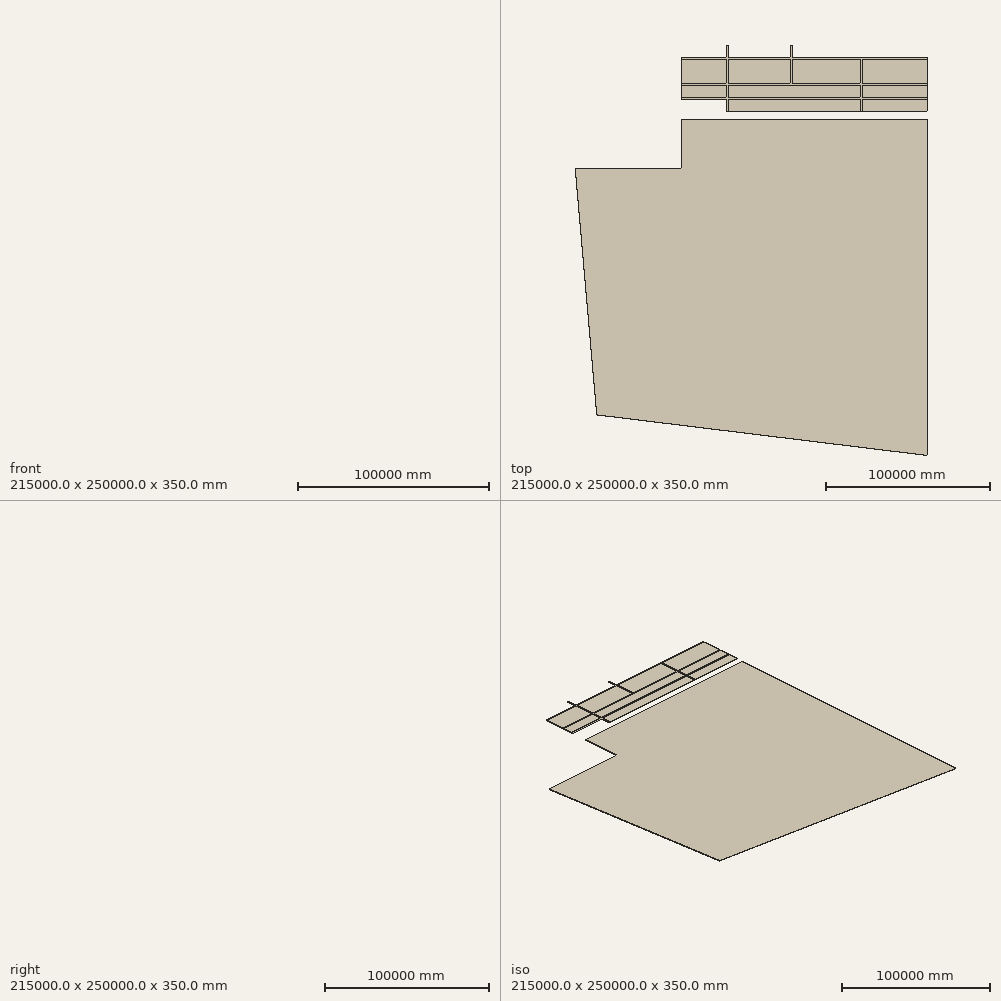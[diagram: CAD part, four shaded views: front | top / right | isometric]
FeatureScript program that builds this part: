
annotation { "Feature Type Name" : "Feature", "Feature Type Description" : "" }
export const myFeature = defineFeature(function(context is Context, id is Id, definition is map)
    precondition{}
    {
        {
            var Q0;
            Q0=qCreatedBy(makeId("Top.planeOp"),FACE);
            var sketch = newSketch(context, id + "F0", { "sketchPlane" : qUnion([Q0])});
            skLineSegment(sketch, "E0.bottom", {"start": v(83751, 27719.32) * mm, "end": v(-66249, 27719.32) * mm});
            skLineSegment(sketch, "E0.top", {"start": v(83751, -12280.68) * mm, "end": v(-66249, -12280.68) * mm});
            skLineSegment(sketch, "E0.right", {"start": v(-66249, 27719.32) * mm, "end": v(-66249, -12280.68) * mm});
            skLineSegment(sketch, "E1", {"start": v(83751, 27719.32) * mm, "end": v(83751, -12280.68) * mm});
            skLineSegment(sketch, "E2.bottom", {"start": v(-66249, 27719.32) * mm, "end": v(-38749, 27719.32) * mm});
            skLineSegment(sketch, "E2.top", {"start": v(-66249, 20439.32) * mm, "end": v(-38749, 20439.32) * mm});
            skLineSegment(sketch, "E2.left", {"start": v(-66249, 27719.32) * mm, "end": v(-66249, 20439.32) * mm});
            skLineSegment(sketch, "E2.right", {"start": v(-38749, 27719.32) * mm, "end": v(-38749, 20439.32) * mm});
            skLineSegment(sketch, "E3.bottom", {"start": v(-37549, 27719.32) * mm, "end": v(-49, 27719.32) * mm});
            skLineSegment(sketch, "E3.top", {"start": v(-37549, 20439.32) * mm, "end": v(-49, 20439.32) * mm});
            skLineSegment(sketch, "E3.left", {"start": v(-37549, 27719.32) * mm, "end": v(-37549, 20439.32) * mm});
            skLineSegment(sketch, "E3.right", {"start": v(-49, 27719.32) * mm, "end": v(-49, 20439.32) * mm});
            skLineSegment(sketch, "E4.bottom", {"start": v(1151, 27719.32) * mm, "end": v(83751, 27719.32) * mm});
            skLineSegment(sketch, "E4.top", {"start": v(1151, 20439.32) * mm, "end": v(83751, 20439.32) * mm});
            skLineSegment(sketch, "E4.left", {"start": v(1151, 27719.32) * mm, "end": v(1151, 20439.32) * mm});
            skLineSegment(sketch, "E5.right", {"start": v(83751, 27719.32) * mm, "end": v(83751, 20439.32) * mm});
            skLineSegment(sketch, "E6", {"start": v(-38749, 20439.32) * mm, "end": v(-37549, 20439.32) * mm, "construction": true});
            skLineSegment(sketch, "E7", {"start": v(-49, 20439.32) * mm, "end": v(1151, 20439.32) * mm, "construction": true});
            skLineSegment(sketch, "E8.bottom", {"start": v(-66249, 4679.32) * mm, "end": v(-38749, 4679.32) * mm});
            skLineSegment(sketch, "E8.top", {"start": v(-66249, 19239.32) * mm, "end": v(-38749, 19239.32) * mm});
            skLineSegment(sketch, "E8.left", {"start": v(-66249, 4679.32) * mm, "end": v(-66249, 19239.32) * mm});
            skLineSegment(sketch, "E8.right", {"start": v(-38749, 4679.32) * mm, "end": v(-38749, 19239.32) * mm});
            skLineSegment(sketch, "E9", {"start": v(-38749, 20439.32) * mm, "end": v(-38749, 19239.32) * mm, "construction": true});
            skLineSegment(sketch, "E10.bottom", {"start": v(-66249, 3479.32) * mm, "end": v(-38749, 3479.32) * mm});
            skLineSegment(sketch, "E10.top", {"start": v(-66249, -3800.68) * mm, "end": v(-38749, -3800.68) * mm});
            skLineSegment(sketch, "E10.left", {"start": v(-66249, 3479.32) * mm, "end": v(-66249, -3800.68) * mm});
            skLineSegment(sketch, "E10.right", {"start": v(-38749, 3479.32) * mm, "end": v(-38749, -3800.68) * mm});
            skLineSegment(sketch, "E11.bottom", {"start": v(-66249, -12280.68) * mm, "end": v(-38749, -12280.68) * mm});
            skLineSegment(sketch, "E11.top", {"start": v(-66249, -5000.68) * mm, "end": v(-38749, -5000.68) * mm});
            skLineSegment(sketch, "E11.left", {"start": v(-66249, -12280.68) * mm, "end": v(-66249, -5000.68) * mm});
            skLineSegment(sketch, "E11.right", {"start": v(-38749, -12280.68) * mm, "end": v(-38749, -5000.68) * mm});
            skLineSegment(sketch, "E12", {"start": v(-38749, -3800.68) * mm, "end": v(-38749, -5000.68) * mm, "construction": true});
            skLineSegment(sketch, "E13", {"start": v(-38749, 3479.32) * mm, "end": v(-38749, 4679.32) * mm, "construction": true});
            skLineSegment(sketch, "E14.bottom", {"start": v(42551, 19239.32) * mm, "end": v(1151, 19239.32) * mm});
            skLineSegment(sketch, "E14.top", {"start": v(42551, 4679.32) * mm, "end": v(1151, 4679.32) * mm});
            skLineSegment(sketch, "E14.left", {"start": v(42551, 19239.32) * mm, "end": v(42551, 4679.32) * mm});
            skLineSegment(sketch, "E14.right", {"start": v(-37549, 19239.32) * mm, "end": v(-37549, 4679.32) * mm});
            skLineSegment(sketch, "E15.bottom", {"start": v(-37549, -3800.68) * mm, "end": v(42551, -3800.68) * mm});
            skLineSegment(sketch, "E15.top", {"start": v(-37549, 3479.32) * mm, "end": v(42551, 3479.32) * mm});
            skLineSegment(sketch, "E15.left", {"start": v(-37549, -3800.68) * mm, "end": v(-37549, 3479.32) * mm});
            skLineSegment(sketch, "E15.right", {"start": v(42551, -3800.68) * mm, "end": v(42551, 3479.32) * mm});
            skLineSegment(sketch, "E16.bottom", {"start": v(-37549, -5000.68) * mm, "end": v(42551, -5000.68) * mm});
            skLineSegment(sketch, "E16.top", {"start": v(-37549, -12280.68) * mm, "end": v(42551, -12280.68) * mm});
            skLineSegment(sketch, "E16.left", {"start": v(-37549, -5000.68) * mm, "end": v(-37549, -12280.68) * mm});
            skLineSegment(sketch, "E16.right", {"start": v(42551, -5000.68) * mm, "end": v(42551, -12280.68) * mm});
            skLineSegment(sketch, "E17.bottom", {"start": v(43751, 19239.32) * mm, "end": v(83751, 19239.32) * mm});
            skLineSegment(sketch, "E17.top", {"start": v(43751, 4679.32) * mm, "end": v(83751, 4679.32) * mm});
            skLineSegment(sketch, "E17.left", {"start": v(43751, 19239.32) * mm, "end": v(43751, 4679.32) * mm});
            skLineSegment(sketch, "E17.right", {"start": v(83751, 19239.32) * mm, "end": v(83751, 4679.32) * mm});
            skLineSegment(sketch, "E18.bottom", {"start": v(43751, 3479.32) * mm, "end": v(83751, 3479.32) * mm});
            skLineSegment(sketch, "E18.top", {"start": v(43751, -3800.68) * mm, "end": v(83751, -3800.68) * mm});
            skLineSegment(sketch, "E18.left", {"start": v(43751, 3479.32) * mm, "end": v(43751, -3800.68) * mm});
            skLineSegment(sketch, "E18.right", {"start": v(83751, 3479.32) * mm, "end": v(83751, -3800.68) * mm});
            skLineSegment(sketch, "E19.bottom", {"start": v(43751, -5000.68) * mm, "end": v(83751, -5000.68) * mm});
            skLineSegment(sketch, "E19.top", {"start": v(43751, -12280.68) * mm, "end": v(83751, -12280.68) * mm});
            skLineSegment(sketch, "E19.left", {"start": v(43751, -5000.68) * mm, "end": v(43751, -12280.68) * mm});
            skLineSegment(sketch, "E19.right", {"start": v(83751, -5000.68) * mm, "end": v(83751, -12280.68) * mm});
            skLineSegment(sketch, "E20", {"start": v(42551, 19239.32) * mm, "end": v(43751, 19239.32) * mm, "construction": true});
            skLineSegment(sketch, "E21", {"start": v(-49, 19239.32) * mm, "end": v(-49, 4679.32) * mm});
            skLineSegment(sketch, "E22", {"start": v(1151, 4679.32) * mm, "end": v(1151, 19239.32) * mm});
            skLineSegment(sketch, "E23.trimOffspring", {"start": v(-49, 4679.32) * mm, "end": v(-37549, 4679.32) * mm});
            skLineSegment(sketch, "E24.trimOffspring", {"start": v(-49, 19239.32) * mm, "end": v(-37549, 19239.32) * mm});
            skSolve(sketch);
        }
        {
            var Q0;
            Q0=qCreatedBy(makeId("Top.planeOp"),FACE);
            var sketch = newSketch(context, id + "F1", { "sketchPlane" : qUnion([Q0])});
            skPoint(sketch, "E25.0", {"position": v(-66249, 27719.32) * mm});
            skPoint(sketch, "E26.0", {"position": v(83751, -12280.68) * mm});
            skPoint(sketch, "E27.0", {"position": v(83751, 27719.32) * mm});
            skPoint(sketch, "E28.0", {"position": v(-66249, -12280.68) * mm});
            skLineSegment(sketch, "E29.bottom", {"start": v(-66249, 27719.32) * mm, "end": v(83751, 27719.32) * mm});
            skLineSegment(sketch, "E29.top", {"start": v(-118106.89, -197495.65) * mm, "end": v(83751, -222280.68) * mm});
            skLineSegment(sketch, "E29.left", {"start": v(-66249, 27719.32) * mm, "end": v(-66249, -47280.68) * mm});
            skLineSegment(sketch, "E29.right", {"start": v(83751, 27719.32) * mm, "end": v(83751, -222280.68) * mm});
            skLineSegment(sketch, "E30.top", {"start": v(-66249, -47280.68) * mm, "end": v(-131249, -47280.68) * mm});
            skLineSegment(sketch, "E30.right", {"start": v(-118106.89, -197495.65) * mm, "end": v(-131249, -47280.68) * mm});
            skSolve(sketch);
        }
        {
            var Q0;
            Q0=qCreatedBy(makeId("Top.planeOp"),FACE);
            var sketch = newSketch(context, id + "F2", { "sketchPlane" : qUnion([Q0])});
            skLineSegment(sketch, "E31.0", {"start": v(-66249, 27719.32) * mm, "end": v(-66249, -47280.68) * mm});
            skLineSegment(sketch, "E32.0", {"start": v(-66249, -47280.68) * mm, "end": v(-131249, -47280.68) * mm});
            skLineSegment(sketch, "E33.0", {"start": v(-118106.89, -197495.65) * mm, "end": v(-131249, -47280.68) * mm});
            skLineSegment(sketch, "E34.0", {"start": v(-118106.89, -197495.65) * mm, "end": v(83751, -222280.68) * mm});
            skLineSegment(sketch, "E35.0", {"start": v(83751, 27719.32) * mm, "end": v(83751, -222280.68) * mm});
            skLineSegment(sketch, "E36", {"start": v(-66249, -17280.68) * mm, "end": v(83751, -17280.68) * mm});
            skLineSegment(sketch, "E37.0", {"start": v(83751, -12280.68) * mm, "end": v(-66249, -12280.68) * mm, "construction": true});
            skSolve(sketch);
        }
        {
            var Q0;
            Q0=makeQuery(id+"F0.imprint","IMPRINT",FACE,{"disambiguationData":[TD([[makeQuery(id+"F0.imprint","IMPRINT",EDGE,{"derivedFrom":sQuery(id+"F0.wireOp",EDGE,"E0.bottom")}),1.0]])]});
            extrude(context, id + "F3", {"entities" : qUnion([Q0]), "depth" : 25 * mm});
        }
        {
            var Q0;
            Q0=makeQuery(id+"F0.imprint","IMPRINT",FACE,{"disambiguationData":[TD([[makeQuery(id+"F0.imprint","IMPRINT",EDGE,{"derivedFrom":sQuery(id+"F0.wireOp",EDGE,"mpzaKtPl-sMag-B9J9-wzII-xAJUliM5p1Ow.bottom")}),-1.0]])]});
            var Q1;
            Q1=makeQuery(id+"F0.imprint","IMPRINT",FACE,{"disambiguationData":[TD([[makeQuery(id+"F0.imprint","IMPRINT",EDGE,{"derivedFrom":sQuery(id+"F0.wireOp",EDGE,"O7xBgzFG-8kGO-UYsZ-ShFJ-g4fqmQPHFW8f.bottom")}),-1.0]])]});
            var Q2;
            Q2=makeQuery(id+"F0.imprint","IMPRINT",FACE,{"disambiguationData":[TD([[makeQuery(id+"F0.imprint","IMPRINT",EDGE,{"derivedFrom":sQuery(id+"F0.wireOp",EDGE,"M8zYxZRN-ssnb-n02M-efZg-0HoLAbz5BKKH.bottom")}),1.0]])]});
            var Q3;
            Q3=makeQuery(id+"F0.imprint","IMPRINT",FACE,{"disambiguationData":[TD([[makeQuery(id+"F0.imprint","IMPRINT",EDGE,{"derivedFrom":sQuery(id+"F0.wireOp",EDGE,"E11.bottom")}),1.0]])]});
            var Q4;
            Q4=makeQuery(id+"F0.imprint","IMPRINT",FACE,{"disambiguationData":[TD([[makeQuery(id+"F0.imprint","IMPRINT",EDGE,{"derivedFrom":sQuery(id+"F0.wireOp",EDGE,"E3.bottom")}),-1.0]])]});
            var Q5;
            Q5=makeQuery(id+"F0.imprint","IMPRINT",FACE,{"disambiguationData":[TD([[makeQuery(id+"F0.imprint","IMPRINT",EDGE,{"derivedFrom":sQuery(id+"F0.wireOp",EDGE,"E17.bottom")}),-1.0]])]});
            extrude(context, id + "F4", {"entities" : qUnion([Q0, Q1, Q2, Q3, Q4, Q5]), "depth" : 350 * mm, "hasSecondDirection" : true, "secondDirectionOppositeDirection" : false, "secondDirectionDepth" : 280 * mm});
        }
        {
            var Q0;
            Q0=makeQuery(id+"F0.imprint","IMPRINT",FACE,{"disambiguationData":[TD([[makeQuery(id+"F0.imprint","IMPRINT",EDGE,{"derivedFrom":sQuery(id+"F0.wireOp",EDGE,"KiBYKJdY-kYvj-F9lR-OJYC-xSlrjwrAbaCp.bottom")}),-1.0]])]});
            var Q1;
            Q1=makeQuery(id+"F0.imprint","IMPRINT",FACE,{"disambiguationData":[TD([[makeQuery(id+"F0.imprint","IMPRINT",EDGE,{"derivedFrom":sQuery(id+"F0.wireOp",EDGE,"vg9kYSW1-ivZH-CJS7-wKYO-tgb2B8ZUoM2v.bottom")}),-1.0]])]});
            var Q2;
            Q2=makeQuery(id+"F0.imprint","IMPRINT",FACE,{"disambiguationData":[TD([[makeQuery(id+"F0.imprint","IMPRINT",EDGE,{"derivedFrom":sQuery(id+"F0.wireOp",EDGE,"6L8BV6vU-2awD-xBSS-NrcB-bH7ilTijgLuj.bottom")}),-1.0]])]});
            var Q3;
            Q3=makeQuery(id+"F0.imprint","IMPRINT",FACE,{"disambiguationData":[TD([[makeQuery(id+"F0.imprint","IMPRINT",EDGE,{"derivedFrom":sQuery(id+"F0.wireOp",EDGE,"3jgzi8BI-OVlr-lQbE-UG3I-K55SZCUtOiHo.bottom")}),-1.0]])]});
            var Q4;
            Q4=makeQuery(id+"F0.imprint","IMPRINT",FACE,{"disambiguationData":[TD([[makeQuery(id+"F0.imprint","IMPRINT",EDGE,{"derivedFrom":sQuery(id+"F0.wireOp",EDGE,"vd8LHleY-lnvj-RdjM-qhDa-UZxHxRBftC3v.bottom")}),-1.0]])]});
            var Q5;
            Q5=makeQuery(id+"F0.imprint","IMPRINT",FACE,{"disambiguationData":[TD([[makeQuery(id+"F0.imprint","IMPRINT",EDGE,{"derivedFrom":sQuery(id+"F0.wireOp",EDGE,"H28q6tYv-c15p-PoiO-Syce-3bSkdqle6fQ7.bottom")}),-1.0]])]});
            var Q6;
            Q6=makeQuery(id+"F0.imprint","IMPRINT",FACE,{"disambiguationData":[TD([[makeQuery(id+"F0.imprint","IMPRINT",EDGE,{"derivedFrom":sQuery(id+"F0.wireOp",EDGE,"E16.bottom")}),-1.0]])]});
            var Q7;
            Q7=makeQuery(id+"F0.imprint","IMPRINT",FACE,{"disambiguationData":[TD([[makeQuery(id+"F0.imprint","IMPRINT",EDGE,{"derivedFrom":sQuery(id+"F0.wireOp",EDGE,"E2.bottom")}),-1.0]])]});
            extrude(context, id + "F5", {"entities" : qUnion([Q0, Q1, Q2, Q3, Q4, Q5, Q6, Q7]), "depth" : 350 * mm, "hasSecondDirection" : true, "secondDirectionOppositeDirection" : false, "secondDirectionDepth" : 280 * mm});
        }
        {
            var Q0;
            Q0=makeQuery(id+"F0.imprint","IMPRINT",FACE,{"disambiguationData":[TD([[makeQuery(id+"F0.imprint","IMPRINT",EDGE,{"derivedFrom":sQuery(id+"F0.wireOp",EDGE,"Jbwq7opg-OvYK-dUf3-kcT7-RQC4l8ZRFqLD.bottom")}),-1.0]])]});
            var Q1;
            Q1=makeQuery(id+"F0.imprint","IMPRINT",FACE,{"disambiguationData":[TD([[makeQuery(id+"F0.imprint","IMPRINT",EDGE,{"derivedFrom":sQuery(id+"F0.wireOp",EDGE,"a7miQCG1-TPCi-mxSo-9yjT-Nva0iuxONBSu.bottom")}),-1.0]])]});
            var Q2;
            Q2=makeQuery(id+"F0.imprint","IMPRINT",FACE,{"disambiguationData":[TD([[makeQuery(id+"F0.imprint","IMPRINT",EDGE,{"derivedFrom":sQuery(id+"F0.wireOp",EDGE,"mVMoQ9I5-IXdS-PVM1-IX5h-BqWUIwhMqsFh.bottom")}),-1.0]])]});
            var Q3;
            Q3=makeQuery(id+"F0.imprint","IMPRINT",FACE,{"disambiguationData":[TD([[makeQuery(id+"F0.imprint","IMPRINT",EDGE,{"derivedFrom":sQuery(id+"F0.wireOp",EDGE,"02QeaROm-5uAY-EsK5-ePjw-ljW041OZLOQT.bottom")}),-1.0]])]});
            var Q4;
            Q4=makeQuery(id+"F0.imprint","IMPRINT",FACE,{"disambiguationData":[TD([[makeQuery(id+"F0.imprint","IMPRINT",EDGE,{"derivedFrom":sQuery(id+"F0.wireOp",EDGE,"E15.bottom")}),1.0]])]});
            var Q5;
            Q5=makeQuery(id+"F0.imprint","IMPRINT",FACE,{"disambiguationData":[TD([[makeQuery(id+"F0.imprint","IMPRINT",EDGE,{"derivedFrom":sQuery(id+"F0.wireOp",EDGE,"E4.bottom")}),-1.0]])]});
            extrude(context, id + "F6", {"entities" : qUnion([Q0, Q1, Q2, Q3, Q4, Q5]), "depth" : 350 * mm, "hasSecondDirection" : true, "secondDirectionOppositeDirection" : false, "secondDirectionDepth" : 280 * mm});
        }
        {
            var Q0;
            Q0=makeQuery(id+"F0.imprint","IMPRINT",FACE,{"disambiguationData":[TD([[makeQuery(id+"F0.imprint","IMPRINT",EDGE,{"derivedFrom":sQuery(id+"F0.wireOp",EDGE,"jMKW8wj7-mqVC-cm2O-JZzu-fpWKkxSADYco.bottom")}),-1.0]])]});
            var Q1;
            Q1=makeQuery(id+"F0.imprint","IMPRINT",FACE,{"disambiguationData":[TD([[makeQuery(id+"F0.imprint","IMPRINT",EDGE,{"derivedFrom":sQuery(id+"F0.wireOp",EDGE,"I21hi6uc-hxY4-hG4o-2rfl-3VSokEDSZXXY.bottom")}),-1.0]])]});
            var Q2;
            Q2=makeQuery(id+"F0.imprint","IMPRINT",FACE,{"disambiguationData":[TD([[makeQuery(id+"F0.imprint","IMPRINT",EDGE,{"derivedFrom":sQuery(id+"F0.wireOp",EDGE,"N7SUgfKg-l1c6-na7o-3wHo-Nj2CwXAmHH9R.bottom")}),-1.0]])]});
            var Q3;
            Q3=makeQuery(id+"F0.imprint","IMPRINT",FACE,{"disambiguationData":[TD([[makeQuery(id+"F0.imprint","IMPRINT",EDGE,{"derivedFrom":sQuery(id+"F0.wireOp",EDGE,"TpX8FIsZ-EkrE-GZDy-pjDt-Fdak3cjo7cPH.bottom")}),-1.0]])]});
            var Q4;
            Q4=makeQuery(id+"F0.imprint","IMPRINT",FACE,{"disambiguationData":[TD([[makeQuery(id+"F0.imprint","IMPRINT",EDGE,{"derivedFrom":sQuery(id+"F0.wireOp",EDGE,"Kw3C1YRV-BLJv-jcxw-njTs-Pnnvmc2v7I7X.bottom")}),-1.0]])]});
            var Q5;
            Q5=makeQuery(id+"F0.imprint","IMPRINT",FACE,{"disambiguationData":[TD([[makeQuery(id+"F0.imprint","IMPRINT",EDGE,{"derivedFrom":sQuery(id+"F0.wireOp",EDGE,"uD0TdgI5-xIzw-Ghip-gELe-p71sjRAgr5fL.bottom")}),-1.0]])]});
            var Q6;
            Q6=makeQuery(id+"F0.imprint","IMPRINT",FACE,{"disambiguationData":[TD([[makeQuery(id+"F0.imprint","IMPRINT",EDGE,{"derivedFrom":sQuery(id+"F0.wireOp",EDGE,"uMdCMPxt-uBFF-KCPK-4fch-RhiwMwN4YdeS.bottom")}),-1.0]])]});
            var Q7;
            Q7=makeQuery(id+"F0.imprint","IMPRINT",FACE,{"disambiguationData":[TD([[makeQuery(id+"F0.imprint","IMPRINT",EDGE,{"derivedFrom":sQuery(id+"F0.wireOp",EDGE,"y34fEfhf-YNB2-dPPO-ACO6-h9ZeJtRRW6us.bottom")}),-1.0]])]});
            var Q8;
            Q8=makeQuery(id+"F0.imprint","IMPRINT",FACE,{"disambiguationData":[TD([[makeQuery(id+"F0.imprint","IMPRINT",EDGE,{"derivedFrom":sQuery(id+"F0.wireOp",EDGE,"0ZgPEorm-4LCI-DBni-WZZm-1QyODzkuBmcz.bottom")}),-1.0]])]});
            var Q9;
            Q9=makeQuery(id+"F0.imprint","IMPRINT",FACE,{"disambiguationData":[TD([[makeQuery(id+"F0.imprint","IMPRINT",EDGE,{"derivedFrom":sQuery(id+"F0.wireOp",EDGE,"qeog7djS-qbvd-LKNM-Kt7P-7ayxPG3yenkM.bottom")}),-1.0]])]});
            var Q10;
            Q10=makeQuery(id+"F0.imprint","IMPRINT",FACE,{"disambiguationData":[TD([[makeQuery(id+"F0.imprint","IMPRINT",EDGE,{"derivedFrom":sQuery(id+"F0.wireOp",EDGE,"sTUXziUP-4wJp-Jmtm-SZMX-pmWH8QZPvHmd.bottom")}),-1.0]])]});
            var Q11;
            Q11=makeQuery(id+"F0.imprint","IMPRINT",FACE,{"disambiguationData":[TD([[makeQuery(id+"F0.imprint","IMPRINT",EDGE,{"derivedFrom":sQuery(id+"F0.wireOp",EDGE,"BGJeclXF-WVl8-qYWH-RyUg-eDzAVnIMdfhu.bottom")}),-1.0]])]});
            var Q12;
            Q12=makeQuery(id+"F0.imprint","IMPRINT",FACE,{"disambiguationData":[TD([[makeQuery(id+"F0.imprint","IMPRINT",EDGE,{"derivedFrom":sQuery(id+"F0.wireOp",EDGE,"YijoEm5l-GGqp-XMXK-bH6d-XAOkhUeKr5JM.bottom")}),-1.0]])]});
            var Q13;
            Q13=makeQuery(id+"F0.imprint","IMPRINT",FACE,{"disambiguationData":[TD([[makeQuery(id+"F0.imprint","IMPRINT",EDGE,{"derivedFrom":sQuery(id+"F0.wireOp",EDGE,"KeLeLgit-TbH1-dZ4Q-9Los-Yp1Dky0e4N30.bottom")}),-1.0]])]});
            var Q14;
            Q14=makeQuery(id+"F0.imprint","IMPRINT",FACE,{"disambiguationData":[TD([[makeQuery(id+"F0.imprint","IMPRINT",EDGE,{"derivedFrom":sQuery(id+"F0.wireOp",EDGE,"lQo1tte5-cMYb-LXfs-VsaY-Ie8Tjb5HG7Dk.bottom")}),-1.0]])]});
            var Q15;
            Q15=makeQuery(id+"F0.imprint","IMPRINT",FACE,{"disambiguationData":[TD([[makeQuery(id+"F0.imprint","IMPRINT",EDGE,{"derivedFrom":sQuery(id+"F0.wireOp",EDGE,"ngXhraBC-Qxv5-AOgt-jkRQ-0wcRXJlRLbNa.bottom")}),-1.0]])]});
            var Q16;
            Q16=makeQuery(id+"F0.imprint","IMPRINT",FACE,{"disambiguationData":[TD([[makeQuery(id+"F0.imprint","IMPRINT",EDGE,{"derivedFrom":sQuery(id+"F0.wireOp",EDGE,"g3wwPQZS-RlxH-GQqO-9bwP-gefgF9dhk7tC.bottom")}),-1.0]])]});
            var Q17;
            Q17=makeQuery(id+"F0.imprint","IMPRINT",FACE,{"disambiguationData":[TD([[makeQuery(id+"F0.imprint","IMPRINT",EDGE,{"derivedFrom":sQuery(id+"F0.wireOp",EDGE,"E19.bottom")}),-1.0]])]});
            var Q18;
            Q18=makeQuery(id+"F0.imprint","IMPRINT",FACE,{"disambiguationData":[TD([[makeQuery(id+"F0.imprint","IMPRINT",EDGE,{"derivedFrom":sQuery(id+"F0.wireOp",EDGE,"E18.bottom")}),-1.0]])]});
            var Q19;
            Q19=makeQuery(id+"F0.imprint","IMPRINT",FACE,{"disambiguationData":[TD([[makeQuery(id+"F0.imprint","IMPRINT",EDGE,{"derivedFrom":sQuery(id+"F0.wireOp",EDGE,"E14.bottom")}),1.0]])]});
            var Q20;
            Q20=makeQuery(id+"F0.imprint","IMPRINT",FACE,{"disambiguationData":[TD([[makeQuery(id+"F0.imprint","IMPRINT",EDGE,{"derivedFrom":sQuery(id+"F0.wireOp",EDGE,"E14.right")}),1.0]])]});
            var Q21;
            Q21=makeQuery(id+"F0.imprint","IMPRINT",FACE,{"disambiguationData":[TD([[makeQuery(id+"F0.imprint","IMPRINT",EDGE,{"derivedFrom":sQuery(id+"F0.wireOp",EDGE,"E8.bottom")}),1.0]])]});
            var Q22;
            Q22=makeQuery(id+"F0.imprint","IMPRINT",FACE,{"disambiguationData":[TD([[makeQuery(id+"F0.imprint","IMPRINT",EDGE,{"derivedFrom":sQuery(id+"F0.wireOp",EDGE,"E10.bottom")}),-1.0]])]});
            extrude(context, id + "F7", {"entities" : qUnion([Q0, Q1, Q2, Q3, Q4, Q5, Q6, Q7, Q8, Q9, Q10, Q11, Q12, Q13, Q14, Q15, Q16, Q17, Q18, Q19, Q20, Q21, Q22]), "depth" : 350 * mm, "hasSecondDirection" : true, "secondDirectionOppositeDirection" : false, "secondDirectionDepth" : 280 * mm});
        }
        {
            var Q0;
            Q0=makeQuery(id+"F0.imprint","IMPRINT",FACE,{"disambiguationData":[TD([[makeQuery(id+"F0.imprint","IMPRINT",EDGE,{"derivedFrom":sQuery(id+"F0.wireOp",EDGE,"mpzaKtPl-sMag-B9J9-wzII-xAJUliM5p1Ow.bottom")}),-1.0]])]});
            var Q1;
            Q1=makeQuery(id+"F0.imprint","IMPRINT",FACE,{"disambiguationData":[TD([[makeQuery(id+"F0.imprint","IMPRINT",EDGE,{"derivedFrom":sQuery(id+"F0.wireOp",EDGE,"M8zYxZRN-ssnb-n02M-efZg-0HoLAbz5BKKH.bottom")}),1.0]])]});
            var Q2;
            Q2=makeQuery(id+"F0.imprint","IMPRINT",FACE,{"disambiguationData":[TD([[makeQuery(id+"F0.imprint","IMPRINT",EDGE,{"derivedFrom":sQuery(id+"F0.wireOp",EDGE,"O7xBgzFG-8kGO-UYsZ-ShFJ-g4fqmQPHFW8f.bottom")}),-1.0]])]});
            var Q3;
            Q3=makeQuery(id+"F0.imprint","IMPRINT",FACE,{"disambiguationData":[TD([[makeQuery(id+"F0.imprint","IMPRINT",EDGE,{"derivedFrom":sQuery(id+"F0.wireOp",EDGE,"3jgzi8BI-OVlr-lQbE-UG3I-K55SZCUtOiHo.bottom")}),-1.0]])]});
            var Q4;
            Q4=makeQuery(id+"F0.imprint","IMPRINT",FACE,{"disambiguationData":[TD([[makeQuery(id+"F0.imprint","IMPRINT",EDGE,{"derivedFrom":sQuery(id+"F0.wireOp",EDGE,"s0wA2RgC-g39R-A75Y-Y0pa-B6aqiDg03CHQ.bottom")}),-1.0]])]});
            var Q5;
            Q5=makeQuery(id+"F0.imprint","IMPRINT",FACE,{"disambiguationData":[TD([[makeQuery(id+"F0.imprint","IMPRINT",EDGE,{"derivedFrom":sQuery(id+"F0.wireOp",EDGE,"TpX8FIsZ-EkrE-GZDy-pjDt-Fdak3cjo7cPH.bottom")}),-1.0]])]});
            var Q6;
            Q6=makeQuery(id+"F0.imprint","IMPRINT",FACE,{"disambiguationData":[TD([[makeQuery(id+"F0.imprint","IMPRINT",EDGE,{"derivedFrom":sQuery(id+"F0.wireOp",EDGE,"vd8LHleY-lnvj-RdjM-qhDa-UZxHxRBftC3v.bottom")}),-1.0]])]});
            var Q7;
            Q7=makeQuery(id+"F0.imprint","IMPRINT",FACE,{"disambiguationData":[TD([[makeQuery(id+"F0.imprint","IMPRINT",EDGE,{"derivedFrom":sQuery(id+"F0.wireOp",EDGE,"mVMoQ9I5-IXdS-PVM1-IX5h-BqWUIwhMqsFh.bottom")}),-1.0]])]});
            var Q8;
            Q8=makeQuery(id+"F0.imprint","IMPRINT",FACE,{"disambiguationData":[TD([[makeQuery(id+"F0.imprint","IMPRINT",EDGE,{"derivedFrom":sQuery(id+"F0.wireOp",EDGE,"N7SUgfKg-l1c6-na7o-3wHo-Nj2CwXAmHH9R.bottom")}),-1.0]])]});
            var Q9;
            Q9=makeQuery(id+"F0.imprint","IMPRINT",FACE,{"disambiguationData":[TD([[makeQuery(id+"F0.imprint","IMPRINT",EDGE,{"derivedFrom":sQuery(id+"F0.wireOp",EDGE,"H28q6tYv-c15p-PoiO-Syce-3bSkdqle6fQ7.bottom")}),-1.0]])]});
            var Q10;
            Q10=makeQuery(id+"F0.imprint","IMPRINT",FACE,{"disambiguationData":[TD([[makeQuery(id+"F0.imprint","IMPRINT",EDGE,{"derivedFrom":sQuery(id+"F0.wireOp",EDGE,"I21hi6uc-hxY4-hG4o-2rfl-3VSokEDSZXXY.bottom")}),-1.0]])]});
            var Q11;
            Q11=makeQuery(id+"F0.imprint","IMPRINT",FACE,{"disambiguationData":[TD([[makeQuery(id+"F0.imprint","IMPRINT",EDGE,{"derivedFrom":sQuery(id+"F0.wireOp",EDGE,"02QeaROm-5uAY-EsK5-ePjw-ljW041OZLOQT.bottom")}),-1.0]])]});
            var Q12;
            Q12=makeQuery(id+"F0.imprint","IMPRINT",FACE,{"disambiguationData":[TD([[makeQuery(id+"F0.imprint","IMPRINT",EDGE,{"derivedFrom":sQuery(id+"F0.wireOp",EDGE,"uD0TdgI5-xIzw-Ghip-gELe-p71sjRAgr5fL.bottom")}),-1.0]])]});
            var Q13;
            Q13=makeQuery(id+"F0.imprint","IMPRINT",FACE,{"disambiguationData":[TD([[makeQuery(id+"F0.imprint","IMPRINT",EDGE,{"derivedFrom":sQuery(id+"F0.wireOp",EDGE,"Kw3C1YRV-BLJv-jcxw-njTs-Pnnvmc2v7I7X.bottom")}),-1.0]])]});
            var Q14;
            Q14=makeQuery(id+"F0.imprint","IMPRINT",FACE,{"disambiguationData":[TD([[makeQuery(id+"F0.imprint","IMPRINT",EDGE,{"derivedFrom":sQuery(id+"F0.wireOp",EDGE,"uMdCMPxt-uBFF-KCPK-4fch-RhiwMwN4YdeS.bottom")}),-1.0]])]});
            var Q15;
            Q15=makeQuery(id+"F0.imprint","IMPRINT",FACE,{"disambiguationData":[TD([[makeQuery(id+"F0.imprint","IMPRINT",EDGE,{"derivedFrom":sQuery(id+"F0.wireOp",EDGE,"lQo1tte5-cMYb-LXfs-VsaY-Ie8Tjb5HG7Dk.bottom")}),-1.0]])]});
            var Q16;
            Q16=makeQuery(id+"F0.imprint","IMPRINT",FACE,{"disambiguationData":[TD([[makeQuery(id+"F0.imprint","IMPRINT",EDGE,{"derivedFrom":sQuery(id+"F0.wireOp",EDGE,"KeLeLgit-TbH1-dZ4Q-9Los-Yp1Dky0e4N30.bottom")}),-1.0]])]});
            var Q17;
            Q17=makeQuery(id+"F0.imprint","IMPRINT",FACE,{"disambiguationData":[TD([[makeQuery(id+"F0.imprint","IMPRINT",EDGE,{"derivedFrom":sQuery(id+"F0.wireOp",EDGE,"X9XOL6zC-ZxmE-k0sM-6Uor-3FqJ8AUOafdA.bottom")}),-1.0]])]});
            var Q18;
            Q18=makeQuery(id+"F0.imprint","IMPRINT",FACE,{"disambiguationData":[TD([[makeQuery(id+"F0.imprint","IMPRINT",EDGE,{"derivedFrom":sQuery(id+"F0.wireOp",EDGE,"a7miQCG1-TPCi-mxSo-9yjT-Nva0iuxONBSu.bottom")}),-1.0]])]});
            var Q19;
            Q19=makeQuery(id+"F0.imprint","IMPRINT",FACE,{"disambiguationData":[TD([[makeQuery(id+"F0.imprint","IMPRINT",EDGE,{"derivedFrom":sQuery(id+"F0.wireOp",EDGE,"sTUXziUP-4wJp-Jmtm-SZMX-pmWH8QZPvHmd.bottom")}),-1.0]])]});
            var Q20;
            Q20=makeQuery(id+"F0.imprint","IMPRINT",FACE,{"disambiguationData":[TD([[makeQuery(id+"F0.imprint","IMPRINT",EDGE,{"derivedFrom":sQuery(id+"F0.wireOp",EDGE,"BGJeclXF-WVl8-qYWH-RyUg-eDzAVnIMdfhu.bottom")}),-1.0]])]});
            var Q21;
            Q21=makeQuery(id+"F0.imprint","IMPRINT",FACE,{"disambiguationData":[TD([[makeQuery(id+"F0.imprint","IMPRINT",EDGE,{"derivedFrom":sQuery(id+"F0.wireOp",EDGE,"YijoEm5l-GGqp-XMXK-bH6d-XAOkhUeKr5JM.bottom")}),-1.0]])]});
            var Q22;
            Q22=makeQuery(id+"F0.imprint","IMPRINT",FACE,{"disambiguationData":[TD([[makeQuery(id+"F0.imprint","IMPRINT",EDGE,{"derivedFrom":sQuery(id+"F0.wireOp",EDGE,"0ZgPEorm-4LCI-DBni-WZZm-1QyODzkuBmcz.bottom")}),-1.0]])]});
            var Q23;
            Q23=makeQuery(id+"F0.imprint","IMPRINT",FACE,{"disambiguationData":[TD([[makeQuery(id+"F0.imprint","IMPRINT",EDGE,{"derivedFrom":sQuery(id+"F0.wireOp",EDGE,"y34fEfhf-YNB2-dPPO-ACO6-h9ZeJtRRW6us.bottom")}),-1.0]])]});
            var Q24;
            Q24=makeQuery(id+"F0.imprint","IMPRINT",FACE,{"disambiguationData":[TD([[makeQuery(id+"F0.imprint","IMPRINT",EDGE,{"derivedFrom":sQuery(id+"F0.wireOp",EDGE,"KiBYKJdY-kYvj-F9lR-OJYC-xSlrjwrAbaCp.bottom")}),-1.0]])]});
            var Q25;
            Q25=makeQuery(id+"F0.imprint","IMPRINT",FACE,{"disambiguationData":[TD([[makeQuery(id+"F0.imprint","IMPRINT",EDGE,{"derivedFrom":sQuery(id+"F0.wireOp",EDGE,"9lUfsFhe-MKmE-jacU-uScO-ev1SAuLgJFo9.bottom")}),-1.0]])]});
            var Q26;
            Q26=makeQuery(id+"F0.imprint","IMPRINT",FACE,{"disambiguationData":[TD([[makeQuery(id+"F0.imprint","IMPRINT",EDGE,{"derivedFrom":sQuery(id+"F0.wireOp",EDGE,"vg9kYSW1-ivZH-CJS7-wKYO-tgb2B8ZUoM2v.bottom")}),-1.0]])]});
            var Q27;
            Q27=makeQuery(id+"F0.imprint","IMPRINT",FACE,{"disambiguationData":[TD([[makeQuery(id+"F0.imprint","IMPRINT",EDGE,{"derivedFrom":sQuery(id+"F0.wireOp",EDGE,"qeog7djS-qbvd-LKNM-Kt7P-7ayxPG3yenkM.bottom")}),-1.0]])]});
            var Q28;
            Q28=makeQuery(id+"F0.imprint","IMPRINT",FACE,{"disambiguationData":[TD([[makeQuery(id+"F0.imprint","IMPRINT",EDGE,{"derivedFrom":sQuery(id+"F0.wireOp",EDGE,"jMKW8wj7-mqVC-cm2O-JZzu-fpWKkxSADYco.bottom")}),-1.0]])]});
            var Q29;
            Q29=makeQuery(id+"F0.imprint","IMPRINT",FACE,{"disambiguationData":[TD([[makeQuery(id+"F0.imprint","IMPRINT",EDGE,{"derivedFrom":sQuery(id+"F0.wireOp",EDGE,"Jbwq7opg-OvYK-dUf3-kcT7-RQC4l8ZRFqLD.bottom")}),-1.0]])]});
            var Q30;
            Q30=makeQuery(id+"F0.imprint","IMPRINT",FACE,{"disambiguationData":[TD([[makeQuery(id+"F0.imprint","IMPRINT",EDGE,{"derivedFrom":sQuery(id+"F0.wireOp",EDGE,"g3wwPQZS-RlxH-GQqO-9bwP-gefgF9dhk7tC.bottom")}),-1.0]])]});
            var Q31;
            Q31=makeQuery(id+"F0.imprint","IMPRINT",FACE,{"disambiguationData":[TD([[makeQuery(id+"F0.imprint","IMPRINT",EDGE,{"derivedFrom":sQuery(id+"F0.wireOp",EDGE,"6L8BV6vU-2awD-xBSS-NrcB-bH7ilTijgLuj.bottom")}),-1.0]])]});
            var Q32;
            Q32=makeQuery(id+"F0.imprint","IMPRINT",FACE,{"disambiguationData":[TD([[makeQuery(id+"F0.imprint","IMPRINT",EDGE,{"derivedFrom":sQuery(id+"F0.wireOp",EDGE,"ngXhraBC-Qxv5-AOgt-jkRQ-0wcRXJlRLbNa.bottom")}),-1.0]])]});
            var Q33;
            Q33=makeQuery(id+"F0.imprint","IMPRINT",FACE,{"disambiguationData":[TD([[makeQuery(id+"F0.imprint","IMPRINT",EDGE,{"derivedFrom":sQuery(id+"F0.wireOp",EDGE,"E4.bottom")}),-1.0]])]});
            var Q34;
            Q34=makeQuery(id+"F0.imprint","IMPRINT",FACE,{"disambiguationData":[TD([[makeQuery(id+"F0.imprint","IMPRINT",EDGE,{"derivedFrom":sQuery(id+"F0.wireOp",EDGE,"E17.bottom")}),-1.0]])]});
            var Q35;
            Q35=makeQuery(id+"F0.imprint","IMPRINT",FACE,{"disambiguationData":[TD([[makeQuery(id+"F0.imprint","IMPRINT",EDGE,{"derivedFrom":sQuery(id+"F0.wireOp",EDGE,"E14.bottom")}),1.0]])]});
            var Q36;
            Q36=makeQuery(id+"F0.imprint","IMPRINT",FACE,{"disambiguationData":[TD([[makeQuery(id+"F0.imprint","IMPRINT",EDGE,{"derivedFrom":sQuery(id+"F0.wireOp",EDGE,"E3.bottom")}),-1.0]])]});
            var Q37;
            Q37=makeQuery(id+"F0.imprint","IMPRINT",FACE,{"disambiguationData":[TD([[makeQuery(id+"F0.imprint","IMPRINT",EDGE,{"derivedFrom":sQuery(id+"F0.wireOp",EDGE,"E2.bottom")}),-1.0]])]});
            var Q38;
            Q38=makeQuery(id+"F0.imprint","IMPRINT",FACE,{"disambiguationData":[TD([[makeQuery(id+"F0.imprint","IMPRINT",EDGE,{"derivedFrom":sQuery(id+"F0.wireOp",EDGE,"E8.bottom")}),1.0]])]});
            var Q39;
            Q39=makeQuery(id+"F0.imprint","IMPRINT",FACE,{"disambiguationData":[TD([[makeQuery(id+"F0.imprint","IMPRINT",EDGE,{"derivedFrom":sQuery(id+"F0.wireOp",EDGE,"E10.bottom")}),-1.0]])]});
            var Q40;
            Q40=makeQuery(id+"F0.imprint","IMPRINT",FACE,{"disambiguationData":[TD([[makeQuery(id+"F0.imprint","IMPRINT",EDGE,{"derivedFrom":sQuery(id+"F0.wireOp",EDGE,"E11.bottom")}),1.0]])]});
            var Q41;
            Q41=makeQuery(id+"F0.imprint","IMPRINT",FACE,{"disambiguationData":[TD([[makeQuery(id+"F0.imprint","IMPRINT",EDGE,{"derivedFrom":sQuery(id+"F0.wireOp",EDGE,"E16.bottom")}),-1.0]])]});
            var Q42;
            Q42=makeQuery(id+"F0.imprint","IMPRINT",FACE,{"disambiguationData":[TD([[makeQuery(id+"F0.imprint","IMPRINT",EDGE,{"derivedFrom":sQuery(id+"F0.wireOp",EDGE,"E15.bottom")}),1.0]])]});
            var Q43;
            Q43=makeQuery(id+"F0.imprint","IMPRINT",FACE,{"disambiguationData":[TD([[makeQuery(id+"F0.imprint","IMPRINT",EDGE,{"derivedFrom":sQuery(id+"F0.wireOp",EDGE,"E18.bottom")}),-1.0]])]});
            var Q44;
            Q44=makeQuery(id+"F0.imprint","IMPRINT",FACE,{"disambiguationData":[TD([[makeQuery(id+"F0.imprint","IMPRINT",EDGE,{"derivedFrom":sQuery(id+"F0.wireOp",EDGE,"E19.bottom")}),-1.0]])]});
            var Q45;
            Q45=makeQuery(id+"F0.imprint","IMPRINT",FACE,{"disambiguationData":[TD([[makeQuery(id+"F0.imprint","IMPRINT",EDGE,{"derivedFrom":sQuery(id+"F0.wireOp",EDGE,"E14.right")}),1.0]])]});
            extrude(context, id + "F8", {"entities" : qUnion([Q0, Q1, Q2, Q3, Q4, Q5, Q6, Q7, Q8, Q9, Q10, Q11, Q12, Q13, Q14, Q15, Q16, Q17, Q18, Q19, Q20, Q21, Q22, Q23, Q24, Q25, Q26, Q27, Q28, Q29, Q30, Q31, Q32, Q33, Q34, Q35, Q36, Q37, Q38, Q39, Q40, Q41, Q42, Q43, Q44, Q45]), "depth" : 280 * mm});
        }
        {
            var Q0;
            {var subQ1=sQuery(id+"F2.wireOp",EDGE,"E32.0");Q0=makeQuery(id+"F2.imprint","IMPRINT",FACE,{"disambiguationData":[TD([[makeQuery(id+"F2.imprint","IMPRINT",EDGE,{"derivedFrom":subQ1}),1.0]])]});}
            extrude(context, id + "F9", {"entities" : qUnion([Q0]), "depth" : 280 * mm});
        }
    });
